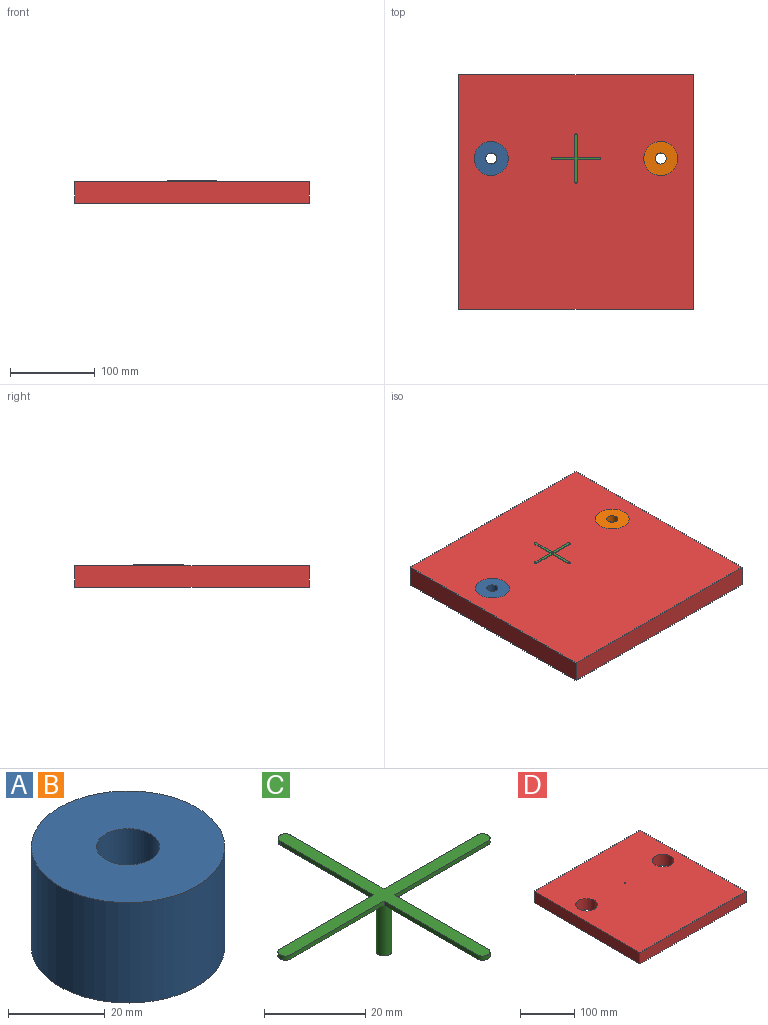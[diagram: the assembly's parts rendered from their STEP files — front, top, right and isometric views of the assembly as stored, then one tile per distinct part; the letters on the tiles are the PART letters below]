
ASSEMBLY  parts=4 mates=3
PART A: 4 faces, bbox 40x40x25.4 mm
  f0: cylinder r=6.5mm len=25.4mm, axis (0,0,-1), area 1037.4mm2, adj f2,f3
  f1: cylinder r=20mm len=40mm, axis (0,0,-1), area 3191.9mm2, adj f2,f3
  f2: plane 40x40mm, normal (0,0,1), area 1123.9mm2, adj f0,f1
  f3: plane 40x40mm, normal (0,0,-1), area 1123.9mm2, adj f0,f1
PART B: same geometry as A
PART C: 16 faces, bbox 58x58x13.7 mm
  f0: cylinder r=1.5mm len=3mm, axis (0,0,-1), area 4.7mm2, adj f1,f11,f12,f13
  f1: plane 26x1mm, normal (0,-1,0), area 26mm2, adj f0,f2,f12,f13
  f2: plane 26x1mm, normal (-1,0,0), area 26mm2, adj f1,f3,f12,f13
  f3: cylinder r=1.5mm len=3mm, axis (0,0,-1), area 4.7mm2, adj f2,f4,f12,f13
  f4: plane 26x1mm, normal (1,0,0), area 26mm2, adj f3,f5,f12,f13
  f5: plane 26x1mm, normal (0,-1,0), area 26mm2, adj f4,f6,f12,f13
  f6: cylinder r=1.5mm len=3mm, axis (0,0,-1), area 4.7mm2, adj f5,f7,f12,f13
  f7: plane 26x1mm, normal (0,1,0), area 26mm2, adj f6,f8,f12,f13
  f8: plane 26x1mm, normal (1,0,0), area 26mm2, adj f7,f9,f12,f13
  f9: cylinder r=1.5mm len=3mm, axis (0,0,-1), area 4.7mm2, adj f8,f10,f12,f13
  f10: plane 26x1mm, normal (-1,0,0), area 26mm2, adj f9,f11,f12,f13
  f11: plane 26x1mm, normal (0,1,0), area 26mm2, adj f0,f10,f12,f13
  f12: plane 58x58mm, normal (0,0,1), area 335.1mm2, adj f0,f1,f2,f3,f4,f5,f6,f7
  f13: plane 58x58mm, normal (0,0,-1), area 327.8mm2, adj f0,f1,f2,f3,f4,f5,f6,f7
  f14: cylinder r=1.52mm len=12.7mm, axis (0,0,1), area 121.6mm2, adj f13,f15
  f15: plane 3.05x3.05mm, normal (0,0,-1), area 7.3mm2, adj f14
PART D: 9 faces, bbox 277x277x25.4 mm
  f0: plane 277x25.4mm, normal (0,1,0), area 7035.8mm2, adj f1,f6,f7,f8
  f1: plane 277x25.4mm, normal (-1,0,0), area 7035.8mm2, adj f0,f2,f7,f8
  f2: plane 277x25.4mm, normal (0,-1,0), area 7035.8mm2, adj f1,f6,f7,f8
  f3: cylinder r=20mm len=40mm, axis (0,0,-1), area 3191.9mm2, adj f7,f8
  f4: cylinder r=1.52mm len=25.4mm, axis (0,0,-1), area 243.2mm2, adj f7,f8
  f5: cylinder r=20mm len=40mm, axis (0,0,-1), area 3191.9mm2, adj f7,f8
  f6: plane 277x25.4mm, normal (1,0,0), area 7035.8mm2, adj f0,f2,f7,f8
  f7: plane 277x277mm, normal (0,0,1), area 74208.4mm2, adj f0,f1,f2,f3,f4,f5,f6
  f8: plane 277x277mm, normal (0,0,-1), area 74208.4mm2, adj f0,f1,f2,f3,f4,f5,f6
PLACE A t=(126.38,67.34,88.74)mm
PLACE B t=(326.38,67.34,88.74)mm
PLACE C t=(226.38,67.34,114.14)mm
PLACE D t=(364.88,166.34,88.74)mm
MATE fastened A.f0 <-> D.f5  axis (0,0,1) through (126.38,67.34,114.14)mm
MATE fastened C.f14 <-> D.f4  axis (0,0,-1) through (226.38,67.34,114.14)mm
MATE fastened B.f1 <-> D.f3  axis (0,0,-1) through (326.38,67.34,114.14)mm
